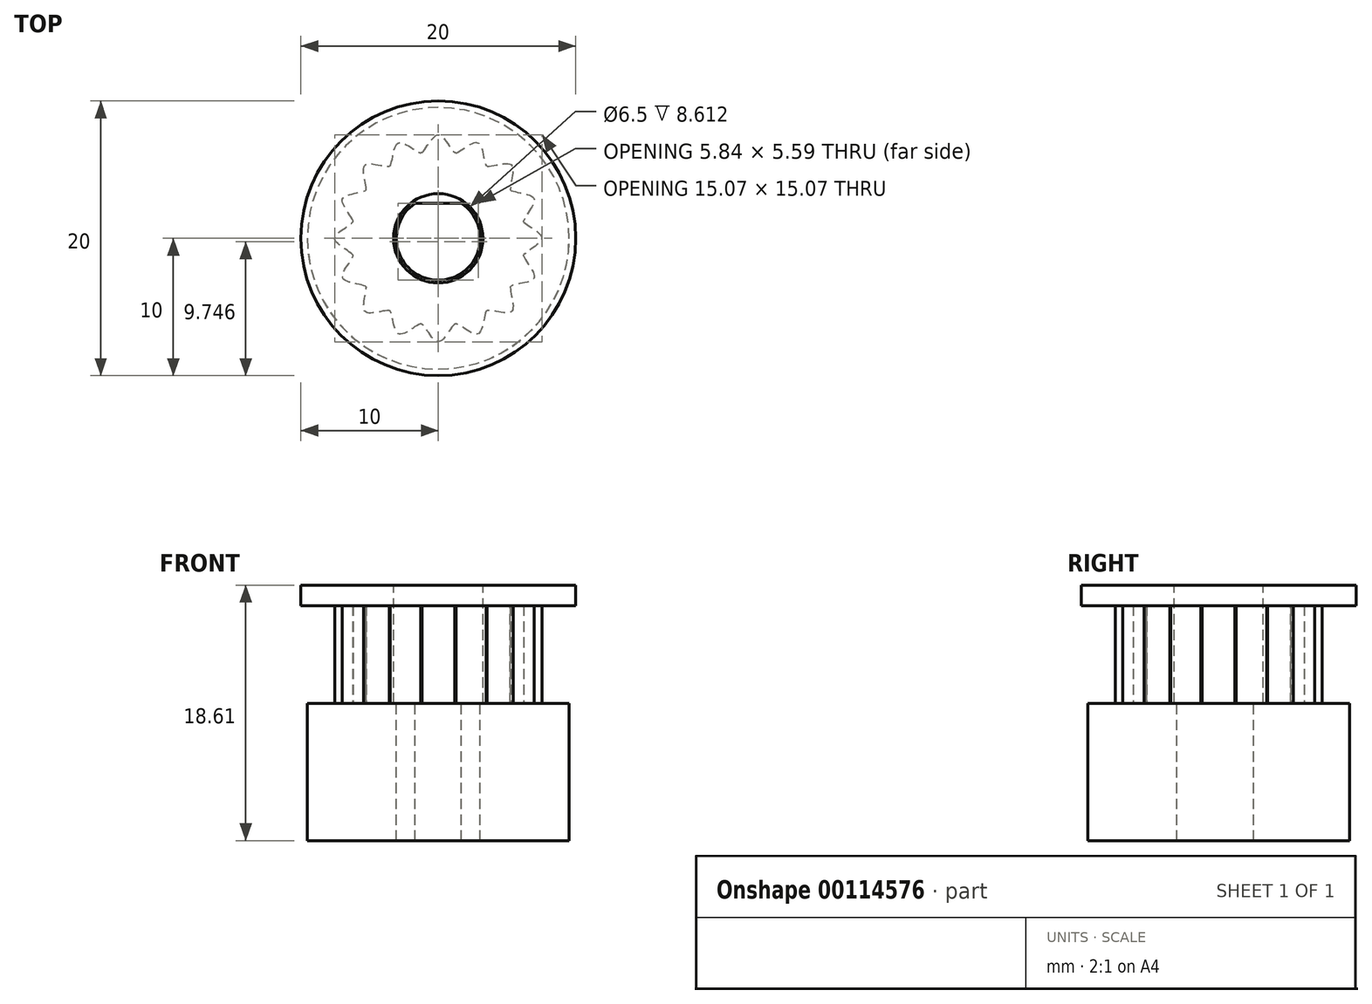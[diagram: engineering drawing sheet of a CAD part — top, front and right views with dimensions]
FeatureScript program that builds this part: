
annotation { "Feature Type Name" : "Feature", "Feature Type Description" : "" }
export const myFeature = defineFeature(function(context is Context, id is Id, definition is map)
    precondition{}
    {
        {
            var Q0;
            Q0=qCreatedBy(makeId("Top.planeOp"),FACE);
            var sketch = newSketch(context, id + "F0", { "sketchPlane" : qUnion([Q0])});
            skCircle(sketch, "E0", {"center": v(0, 0) * mm, "radius": 4.04 * mm});
            skSolve(sketch);
        }
        {
            var Q0;
            Q0 = qSketchRegion(id + "F0", true);
            extrude(context, id + "F1", {"entities" : qUnion([Q0]), "depth" : 10 * mm});
        }
        {
            var Q0;
            Q0=makeQuery(id+"F1.opExtrude","CAP_FACE",FACE,{"disambiguationData":[OSD([sQuery(id+"F0.wireOp",EDGE,"E0")])],"isStart":false});
            var sketch = newSketch(context, id + "F2", { "sketchPlane" : qUnion([Q0])});
            skCircle(sketch, "E1", {"center": v(0, 0) * mm, "radius": 6.34 * mm});
            skFitSpline(sketch, "E2", {"points": [v(-1.2, 6.23) * mm, v(0, 7.53) * mm, v(1.2, 6.23) * mm], "startDerivative": vector(2.23, 2.26) * mm, "endDerivative": vector(2.28, -2.04) * mm});
            skSolve(sketch);
        }
        {
            var Q0;
            Q0 = qSketchRegion(id + "F2", true);
            extrude(context, id + "F3", {"entities" : qUnion([Q0]), "operationType" : NewBodyOperationType.ADD, "depth" : 7.11 * mm});
        }
        {
            var Q0;
            Q0=qCreatedBy(makeId("Front.planeOp"),FACE);
            var sketch = newSketch(context, id + "F4", { "sketchPlane" : qUnion([Q0])});
            skLineSegment(sketch, "E3", {"start": v(0, 0) * mm, "end": v(0, 32.54) * mm});
            skSolve(sketch);
        }
        {
            var Q0;
            Q0=makeQuery(id+"F1.opExtrude","SWEPT_BODY",BODY,{"disambiguationData":[OSD([sQuery(id+"F0.wireOp",EDGE,"E0")])]});
            var Q1;
            Q1=sQuery(id+"F4.wireOp",EDGE,"E3");
            circularPattern(context, id + "F5", {"operationType" : NewBodyOperationType.ADD, "entities" : qUnion([Q0]), "axis" : qUnion([Q1]), "angle" : 360 * degree, "instanceCount" : 16, "equalSpace" : true});
        }
        {
            var Q0;
            {var subQ0=makeQuery(id+"F3.opExtrude","CAP_FACE",FACE,{"disambiguationData":[OSD([sQuery(id+"F2.wireOp",EDGE,"E1"),sQuery(id+"F2.wireOp",EDGE,"E2")])],"isStart":false});Q0=makeQuery(id+"F5.boolean.opBoolean","MERGE",FACE,{"derivedFrom":[subQ0,makeQuery(id+"F5.opPattern","COPY",FACE,{"derivedFrom":subQ0,"instanceName":"1"}),makeQuery(id+"F5.opPattern","COPY",FACE,{"derivedFrom":subQ0,"instanceName":"2"}),makeQuery(id+"F5.opPattern","COPY",FACE,{"derivedFrom":subQ0,"instanceName":"3"}),makeQuery(id+"F5.opPattern","COPY",FACE,{"derivedFrom":subQ0,"instanceName":"4"}),makeQuery(id+"F5.opPattern","COPY",FACE,{"derivedFrom":subQ0,"instanceName":"5"}),makeQuery(id+"F5.opPattern","COPY",FACE,{"derivedFrom":subQ0,"instanceName":"6"}),makeQuery(id+"F5.opPattern","COPY",FACE,{"derivedFrom":subQ0,"instanceName":"7"}),makeQuery(id+"F5.opPattern","COPY",FACE,{"derivedFrom":subQ0,"instanceName":"8"}),makeQuery(id+"F5.opPattern","COPY",FACE,{"derivedFrom":subQ0,"instanceName":"9"}),makeQuery(id+"F5.opPattern","COPY",FACE,{"derivedFrom":subQ0,"instanceName":"10"}),makeQuery(id+"F5.opPattern","COPY",FACE,{"derivedFrom":subQ0,"instanceName":"11"}),makeQuery(id+"F5.opPattern","COPY",FACE,{"derivedFrom":subQ0,"instanceName":"12"}),makeQuery(id+"F5.opPattern","COPY",FACE,{"derivedFrom":subQ0,"instanceName":"13"}),makeQuery(id+"F5.opPattern","COPY",FACE,{"derivedFrom":subQ0,"instanceName":"14"}),makeQuery(id+"F5.opPattern","COPY",FACE,{"derivedFrom":subQ0,"instanceName":"15"})]});}
            var sketch = newSketch(context, id + "F6", { "sketchPlane" : qUnion([Q0])});
            skCircle(sketch, "E4", {"center": v(0, 0) * mm, "radius": 10 * mm});
            skSolve(sketch);
        }
        {
            var Q0;
            Q0 = qSketchRegion(id + "F6", true);
            extrude(context, id + "F7", {"entities" : qUnion([Q0]), "operationType" : NewBodyOperationType.ADD, "depth" : 1.5 * mm});
        }
        {
            var Q0;
            Q0=makeQuery(id+"F7.opExtrude","CAP_FACE",FACE,{"disambiguationData":[OSD([sQuery(id+"F6.wireOp",EDGE,"E4")])],"isStart":false});
            var sketch = newSketch(context, id + "F8", { "sketchPlane" : qUnion([Q0])});
            skCircle(sketch, "E5", {"center": v(0, 0) * mm, "radius": 3.25 * mm});
            skSolve(sketch);
        }
        {
            var Q0;
            Q0 = qSketchRegion(id + "F8", true);
            extrude(context, id + "F9", {"entities" : qUnion([Q0]), "operationType" : NewBodyOperationType.REMOVE, "endBound" : BoundingType.THROUGH_ALL, "oppositeDirection" : true, "depth" : 25.4 * mm});
        }
        {
            var Q0;
            {var subQ0=makeQuery(id+"F3.opExtrude","CAP_FACE",FACE,{"disambiguationData":[OSD([sQuery(id+"F2.wireOp",EDGE,"E1"),sQuery(id+"F2.wireOp",EDGE,"E2")])],"isStart":true});Q0=makeQuery(id+"F5.boolean.opBoolean","MERGE",FACE,{"derivedFrom":[subQ0,makeQuery(id+"F5.opPattern","COPY",FACE,{"derivedFrom":subQ0,"instanceName":"1"}),makeQuery(id+"F5.opPattern","COPY",FACE,{"derivedFrom":subQ0,"instanceName":"2"}),makeQuery(id+"F5.opPattern","COPY",FACE,{"derivedFrom":subQ0,"instanceName":"3"}),makeQuery(id+"F5.opPattern","COPY",FACE,{"derivedFrom":subQ0,"instanceName":"4"}),makeQuery(id+"F5.opPattern","COPY",FACE,{"derivedFrom":subQ0,"instanceName":"5"}),makeQuery(id+"F5.opPattern","COPY",FACE,{"derivedFrom":subQ0,"instanceName":"6"}),makeQuery(id+"F5.opPattern","COPY",FACE,{"derivedFrom":subQ0,"instanceName":"7"}),makeQuery(id+"F5.opPattern","COPY",FACE,{"derivedFrom":subQ0,"instanceName":"8"}),makeQuery(id+"F5.opPattern","COPY",FACE,{"derivedFrom":subQ0,"instanceName":"9"}),makeQuery(id+"F5.opPattern","COPY",FACE,{"derivedFrom":subQ0,"instanceName":"10"}),makeQuery(id+"F5.opPattern","COPY",FACE,{"derivedFrom":subQ0,"instanceName":"11"}),makeQuery(id+"F5.opPattern","COPY",FACE,{"derivedFrom":subQ0,"instanceName":"12"}),makeQuery(id+"F5.opPattern","COPY",FACE,{"derivedFrom":subQ0,"instanceName":"13"}),makeQuery(id+"F5.opPattern","COPY",FACE,{"derivedFrom":subQ0,"instanceName":"14"}),makeQuery(id+"F5.opPattern","COPY",FACE,{"derivedFrom":subQ0,"instanceName":"15"})]});}
            var sketch = newSketch(context, id + "F10", { "sketchPlane" : qUnion([Q0])});
            skCircle(sketch, "E6", {"center": v(0, 0) * mm, "radius": 9.53 * mm});
            skSolve(sketch);
        }
        {
            var Q0;
            Q0 = qSketchRegion(id + "F10", true);
            var Q1;
            Q1=qCreatedBy(makeId("Top.planeOp"),FACE);
            extrude(context, id + "F11", {"entities" : qUnion([Q0]), "operationType" : NewBodyOperationType.ADD, "endBound" : BoundingType.UP_TO_SURFACE, "endBoundEntityFace" : qUnion([Q1]), "depth" : 6.35 * mm});
        }
        {
            var Q0;
            Q0=makeQuery(id+"F7.opExtrude","CAP_FACE",FACE,{"disambiguationData":[OSD([sQuery(id+"F6.wireOp",EDGE,"E4")])],"isStart":false});
            var sketch = newSketch(context, id + "F12", { "sketchPlane" : qUnion([Q0])});
            skArc(sketch, "E7", {"start": v(-1.68, 2.54) * mm, "mid": v(0, -3.05) * mm, "end": v(1.68, 2.54) * mm});
            skLineSegment(sketch, "E8", {"start": v(-1.68, 2.54) * mm, "end": v(1.68, 2.54) * mm});
            skSolve(sketch);
        }
        {
            var Q0;
            Q0 = qSketchRegion(id + "F12", true);
            extrude(context, id + "F13", {"entities" : qUnion([Q0]), "operationType" : NewBodyOperationType.REMOVE, "endBound" : BoundingType.THROUGH_ALL, "oppositeDirection" : true, "depth" : 25.4 * mm});
        }
    });
